# Revit family: Robe_Hook-DXV-Modulus-D35120210_Series
name_source: partatom
category: Specialty Equipment
units: mm (PartAtom-declared; Revit-internal decimal feet)

## family parameters
Cut with Voids When Loaded = No
Host = Face
OmniClass Number = 23.40.20.21.31
OmniClass Title = Robe Hooks
Part Type = Normal
Room Calculation Point = No
Round Connector Dimension = Use Diameter
Shared = Yes

## types (4) — shared parameters
Assembly Code = C1030200
Default Elevation = 48"
Description = DXV Modulus Robe Hook
Height = 3 1/16"
Installation Instruction Link = https://dxv01.blob.core.windows.net
Installation Type = Wall Mounted
Length = 2 1/8"
Manufacturer = DXV
Price = Prices may vary. Please consult Manufacturer Representative for most up-to-date price list.
Product Documentation Link = https://dxv01.blob.core.windows.net
Product Page URL = https://www.dxv.com
Revised Date = 03/07/2022
URL = https://www.dxv.com
Width = 1 3/4"

## per-type parameters (varying)
| type | Finish | Finish 2 | Material |
| D35120210.100 | Brass-DXV-100-Polished Chrome | Brass-DXV-144-Brushed_Nickel | Brass-DXV-100-Polished Chrome |
| D35120210.144 | Brass-DXV-144-Brushed_Nickel | Brass-DXV-100-Polished Chrome | Brass-DXV-144-Brushed Nickel |
| D35120210.150 | Brass-DXV-150-Platinum_Nickel | Brass-DXV-144-Brushed_Nickel | Brass-DXV-150-Platinum Nickel |
| D35120210.243 | Brass-DXV-243-Matte Black | Brass-DXV-Polished Black | Brass-DXV-243-Matte Black |

note: column(s) folded — value = type name in every type: Model

## geometry (parser evidence)
native form markers: Sweep x3
no freeform markers — native parametric forms only
